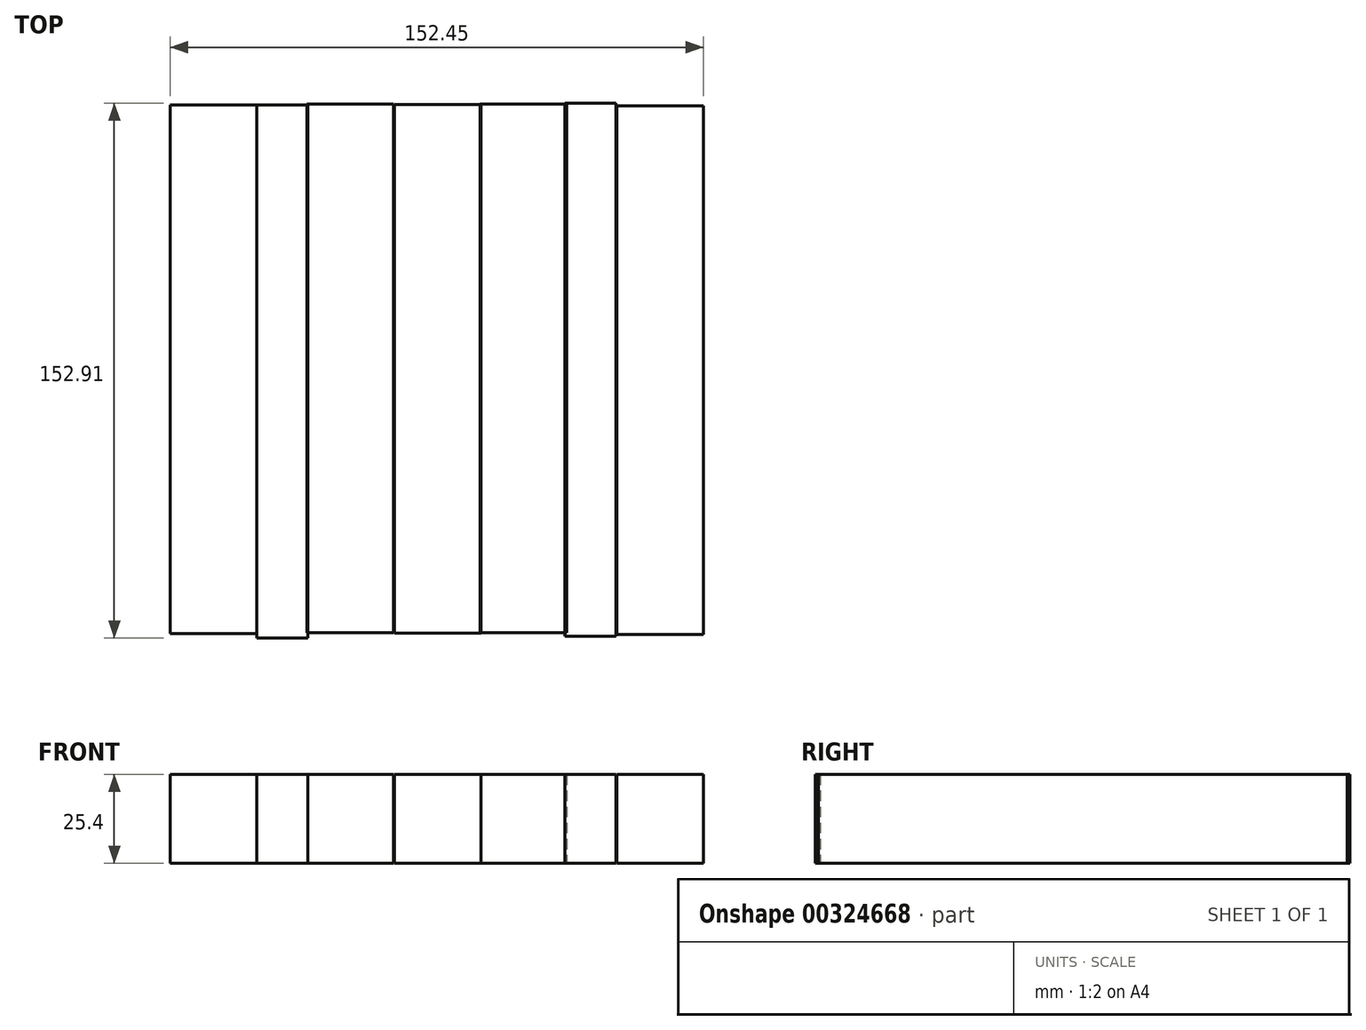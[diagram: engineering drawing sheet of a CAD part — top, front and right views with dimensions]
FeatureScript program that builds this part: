
annotation { "Feature Type Name" : "Feature", "Feature Type Description" : "" }
export const myFeature = defineFeature(function(context is Context, id is Id, definition is map)
    precondition{}
    {
        {
            var Q0;
            Q0=qCreatedBy(makeId("Top.planeOp"),FACE);
            var sketch = newSketch(context, id + "F0", { "sketchPlane" : qUnion([Q0])});
            skLineSegment(sketch, "E0.bottom", {"start": v(-76.5, 75.44) * mm, "end": v(-51.82, 75.44) * mm});
            skLineSegment(sketch, "E0.top", {"start": v(-76.5, -75.74) * mm, "end": v(-51.82, -75.74) * mm});
            skLineSegment(sketch, "E0.left", {"start": v(-76.5, 75.44) * mm, "end": v(-76.5, -75.74) * mm});
            skLineSegment(sketch, "E0.right", {"start": v(-51.82, 75.44) * mm, "end": v(-51.82, -75.74) * mm});
            skSolve(sketch);
        }
        {
            var Q0;
            Q0=makeQuery(id+"F0.imprint","IMPRINT",FACE,{"disambiguationData":[TD([[makeQuery(id+"F0.imprint","IMPRINT",EDGE,{"derivedFrom":sQuery(id+"F0.wireOp",EDGE,"E0.bottom")}),-1.0]])]});
            extrude(context, id + "F1", {"entities" : qUnion([Q0]), "depth" : 25.4 * mm});
        }
        {
            var Q0;
            Q0=qCreatedBy(makeId("Top.planeOp"),FACE);
            var sketch = newSketch(context, id + "F2", { "sketchPlane" : qUnion([Q0])});
            skLineSegment(sketch, "E1.bottom", {"start": v(-12.34, 75.6) * mm, "end": v(12.34, 75.6) * mm});
            skLineSegment(sketch, "E1.top", {"start": v(-12.34, -75.6) * mm, "end": v(12.34, -75.6) * mm});
            skLineSegment(sketch, "E1.left", {"start": v(-12.34, 75.6) * mm, "end": v(-12.34, -75.6) * mm});
            skLineSegment(sketch, "E1.right", {"start": v(12.34, 75.6) * mm, "end": v(12.34, -75.6) * mm});
            skSolve(sketch);
        }
        {
            var Q0;
            Q0=makeQuery(id+"F2.imprint","IMPRINT",FACE,{"disambiguationData":[TD([[makeQuery(id+"F2.imprint","IMPRINT",EDGE,{"derivedFrom":sQuery(id+"F2.wireOp",EDGE,"E1.bottom")}),-1.0]])]});
            extrude(context, id + "F3", {"entities" : qUnion([Q0]), "depth" : 25.4 * mm});
        }
        {
            var Q0;
            Q0=makeQuery(id+"F1.opExtrude","SWEPT_BODY",BODY,{"disambiguationData":[OSD([sQuery(id+"F0.wireOp",EDGE,"E0.bottom"),sQuery(id+"F0.wireOp",EDGE,"E0.top"),sQuery(id+"F0.wireOp",EDGE,"E0.left"),sQuery(id+"F0.wireOp",EDGE,"E0.right")])]});
            transform(context, id + "F4", {"entities" : qUnion([Q0]), "transformType" : TransformType.TRANSLATION_3D, "dx" : 39.12 * mm, "dy" : 0.25 * mm, "dz" : 0 * mm, "makeCopy" : true});
        }
        {
            var Q0;
            Q0=makeQuery(id+"F1.opExtrude","SWEPT_BODY",BODY,{"disambiguationData":[OSD([sQuery(id+"F0.wireOp",EDGE,"E0.bottom"),sQuery(id+"F0.wireOp",EDGE,"E0.top"),sQuery(id+"F0.wireOp",EDGE,"E0.left"),sQuery(id+"F0.wireOp",EDGE,"E0.right")])]});
            transform(context, id + "F5", {"entities" : qUnion([Q0]), "transformType" : TransformType.TRANSLATION_3D, "dx" : 88.65 * mm, "dy" : 0.25 * mm, "dz" : 0 * mm, "makeCopy" : true});
        }
        {
            var Q0;
            Q0=makeQuery(id+"F1.opExtrude","SWEPT_BODY",BODY,{"disambiguationData":[OSD([sQuery(id+"F0.wireOp",EDGE,"E0.bottom"),sQuery(id+"F0.wireOp",EDGE,"E0.top"),sQuery(id+"F0.wireOp",EDGE,"E0.left"),sQuery(id+"F0.wireOp",EDGE,"E0.right")])]});
            transform(context, id + "F6", {"entities" : qUnion([Q0]), "transformType" : TransformType.TRANSLATION_3D, "dx" : 127.76 * mm, "dy" : -0.25 * mm, "dz" : 0 * mm, "makeCopy" : true});
        }
        {
            var Q0;
            Q0=qCreatedBy(makeId("Top.planeOp"),FACE);
            var sketch = newSketch(context, id + "F7", { "sketchPlane" : qUnion([Q0])});
            skLineSegment(sketch, "E2.bottom", {"start": v(-51.82, 75.44) * mm, "end": v(-37.19, 75.44) * mm});
            skLineSegment(sketch, "E2.top", {"start": v(-51.82, -76.96) * mm, "end": v(-37.19, -76.96) * mm});
            skLineSegment(sketch, "E2.left", {"start": v(-51.82, 75.44) * mm, "end": v(-51.82, -76.96) * mm});
            skLineSegment(sketch, "E2.right", {"start": v(-37.19, 75.44) * mm, "end": v(-37.19, -76.96) * mm});
            skSolve(sketch);
        }
        {
            var Q0;
            Q0=makeQuery(id+"F7.imprint","IMPRINT",FACE,{"disambiguationData":[TD([[makeQuery(id+"F7.imprint","IMPRINT",EDGE,{"derivedFrom":sQuery(id+"F7.wireOp",EDGE,"E2.bottom")}),-1.0]])]});
            extrude(context, id + "F8", {"entities" : qUnion([Q0]), "depth" : 25.4 * mm});
        }
        {
            var Q0;
            Q0=makeQuery(id+"F8.opExtrude","SWEPT_BODY",BODY,{"disambiguationData":[OSD([sQuery(id+"F7.wireOp",EDGE,"E2.bottom"),sQuery(id+"F7.wireOp",EDGE,"E2.top"),sQuery(id+"F7.wireOp",EDGE,"E2.left"),sQuery(id+"F7.wireOp",EDGE,"E2.right")])]});
            transform(context, id + "F9", {"entities" : qUnion([Q0]), "transformType" : TransformType.TRANSLATION_3D, "dx" : 88.14 * mm, "dy" : 0.5 * mm, "dz" : 0 * mm, "makeCopy" : true});
        }
    });
